# Revit family: Gira_099600
name_source: partatom
category: Elektroinstallationen
revit_build: Autodesk Revit 2017 (Build: 20160225_1515(x64)
units: mm (PartAtom-declared; Revit-internal decimal feet)

## family parameters
Basisbauteil = Fläche
Beim Laden mit Abzugskörper schneiden = Nein
Bemaßung runder Anschluss = Durchmesser verwenden
Beschriftungsausrichtung beibehalten = Nein
Gemeinsam genutzt = Nein
Raumberechnungspunkt = Nein
Teiletyp = Normal

## types (1)
- Gira_099600
    Anwendung = Schalter/Taster
    BIM = https://media.stage.bim.site
    Beschreibung = Glimmlampenelement 230 V~  0,8 mA
    Datenblatt = https://katalog.gira.de
    Fassung = Stecksockel
    GTIN = 4010337996002
    HAN = 099600
    Hersteller = Gira
    Leuchtmittel = Glimmlampe
    Nennstrom = 0 A
    Nennstromaufnahme = 0 A
    Produktseite = http://katalog.gira.de
    Typname = Glimmlampenelement 0,8 mA Zubehör
    URL = https://www.gira.de
    Vorgabe-Ansicht = 1219 mm

## geometry (parser evidence)
native form markers: Sweep x2
no freeform markers — native parametric forms only
